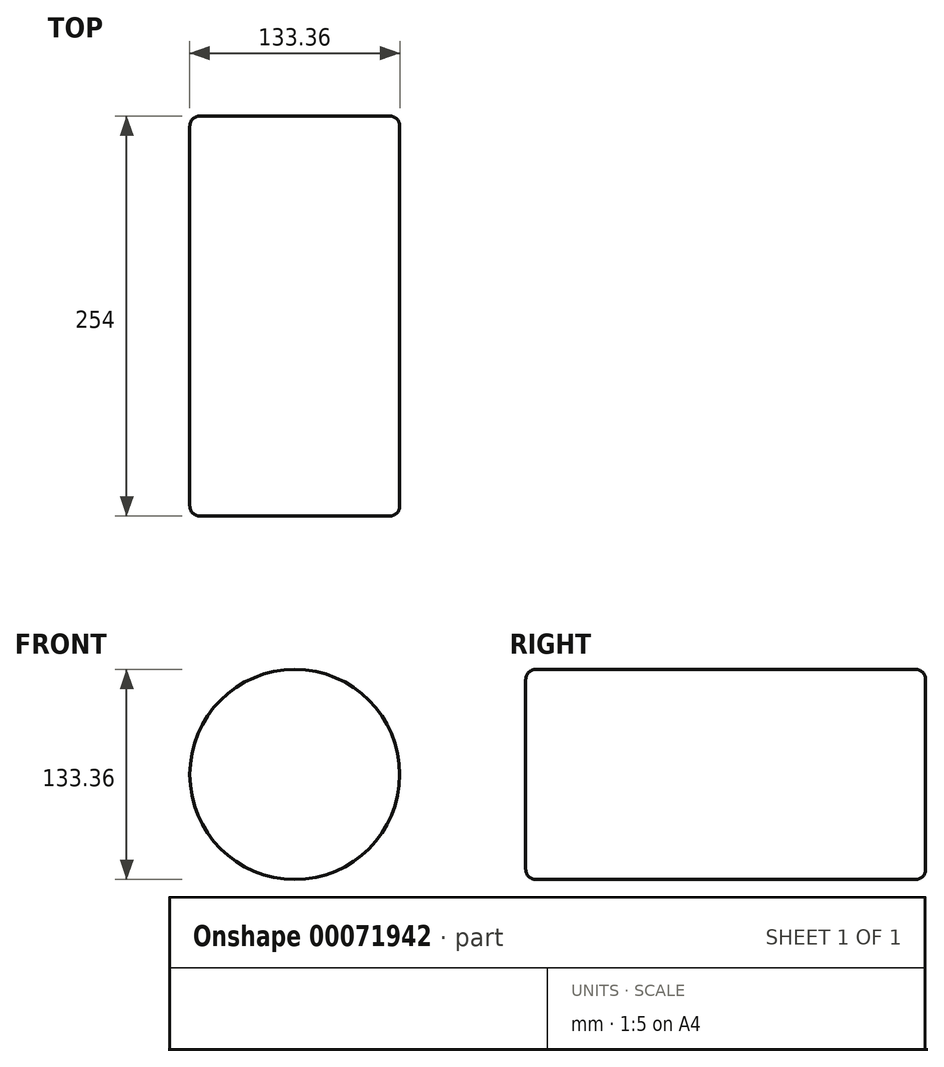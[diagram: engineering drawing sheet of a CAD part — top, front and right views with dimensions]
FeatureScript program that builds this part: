
annotation { "Feature Type Name" : "Feature", "Feature Type Description" : "" }
export const myFeature = defineFeature(function(context is Context, id is Id, definition is map)
    precondition{}
    {
        {
            var Q0;
            Q0=qCreatedBy(makeId("Front.planeOp"),FACE);
            var sketch = newSketch(context, id + "F0", { "sketchPlane" : qUnion([Q0])});
            skCircle(sketch, "E0", {"center": v(0, 0) * mm, "radius": 66.68 * mm});
            skSolve(sketch);
        }
        {
            var Q0;
            Q0=makeQuery(id+"F0.imprint","IMPRINT",FACE,{"disambiguationData":[TD([[makeQuery(id+"F0.imprint","IMPRINT",EDGE,{"derivedFrom":sQuery(id+"F0.wireOp",EDGE,"E0")}),1.0]])]});
            extrude(context, id + "F1", {"entities" : qUnion([Q0]), "depth" : 254 * mm});
        }
        {
            var Q0;
            Q0=makeQuery(id+"F1.opExtrude","CAP_FACE",FACE,{"disambiguationData":[OSD([sQuery(id+"F0.wireOp",EDGE,"E0")])],"isStart":false});
            var Q1;
            Q1=makeQuery(id+"F1.opExtrude","SWEPT_FACE",FACE,{"disambiguationData":[OSD([sQuery(id+"F0.wireOp",EDGE,"E0")])]});
            var Q2;
            Q2=makeQuery(id+"F1.opExtrude","CAP_FACE",FACE,{"disambiguationData":[OSD([sQuery(id+"F0.wireOp",EDGE,"E0")])],"isStart":true});
            fillet(context, id + "F2", {"entities" : qUnion([Q0, Q1, Q2]), "radius" : 6.35 * mm, "tangentPropagation" : true, "allowEdgeOverflow" : false});
        }
    });
